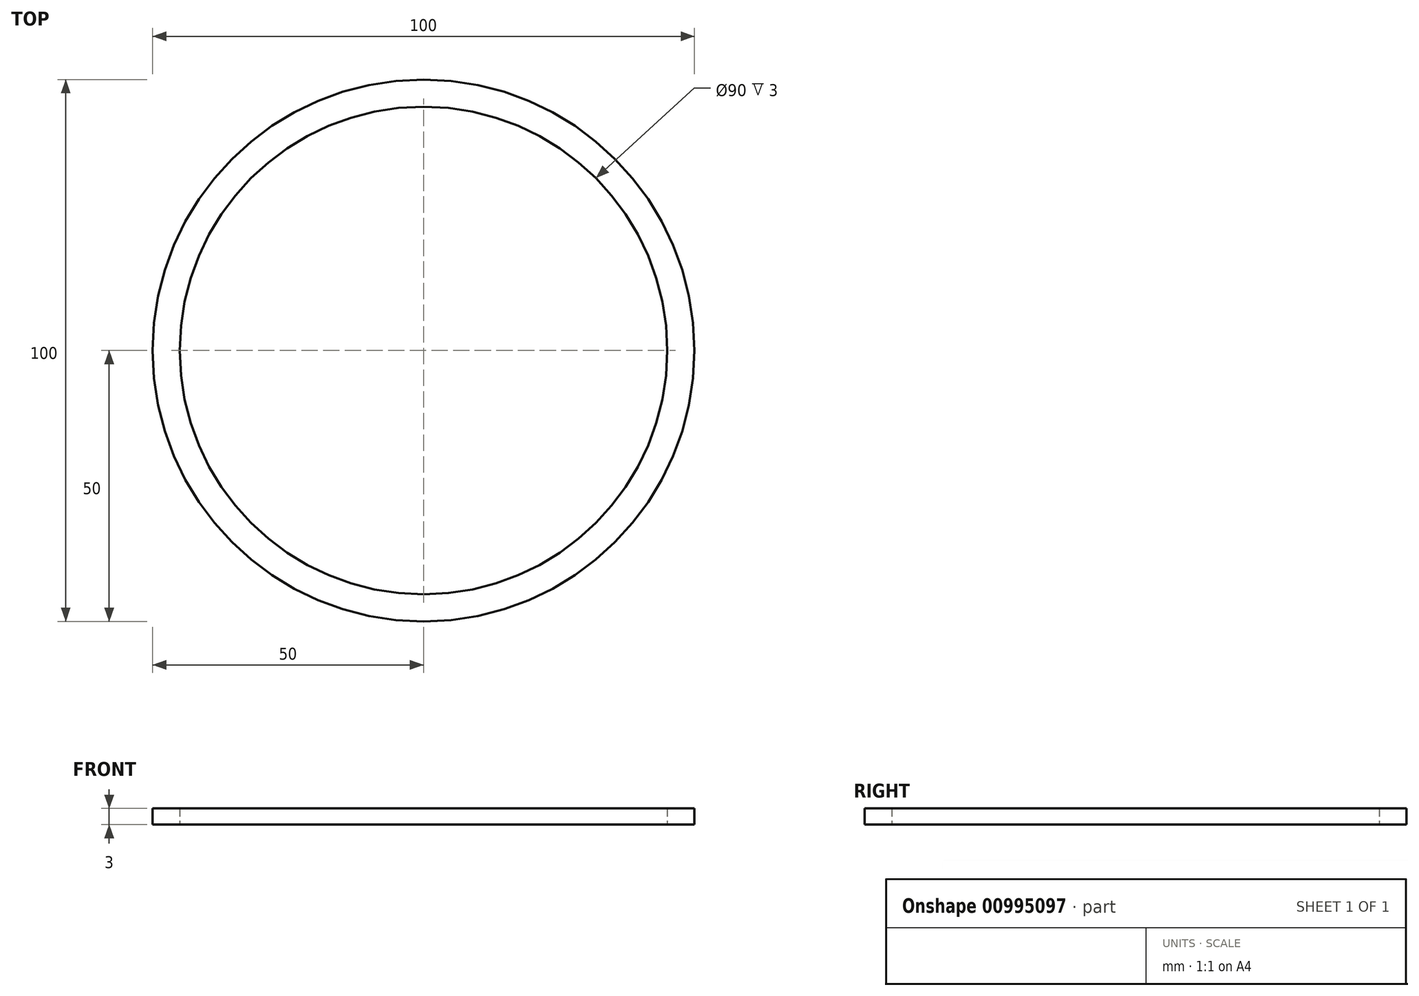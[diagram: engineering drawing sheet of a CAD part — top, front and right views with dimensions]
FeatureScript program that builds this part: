
annotation { "Feature Type Name" : "Feature", "Feature Type Description" : "" }
export const myFeature = defineFeature(function(context is Context, id is Id, definition is map)
    precondition{}
    {
        {
            var Q0;
            Q0=qCreatedBy(makeId("Top.planeOp"),FACE);
            var sketch = newSketch(context, id + "F0", { "sketchPlane" : qUnion([Q0])});
            skCircle(sketch, "E0", {"center": v(0, 0) * mm, "radius": 50 * mm});
            skCircle(sketch, "E1", {"center": v(0, 0) * mm, "radius": 45 * mm});
            skSolve(sketch);
        }
        {
            var Q0;
            Q0=makeQuery(id+"F0.imprint","IMPRINT",FACE,{"disambiguationData":[TD([[makeQuery(id+"F0.imprint","IMPRINT",EDGE,{"derivedFrom":sQuery(id+"F0.wireOp",EDGE,"E0")}),1.0]])]});
            extrude(context, id + "F1", {"entities" : qUnion([Q0]), "depth" : 3 * mm, "offsetDistance" : 25 * mm});
        }
    });
